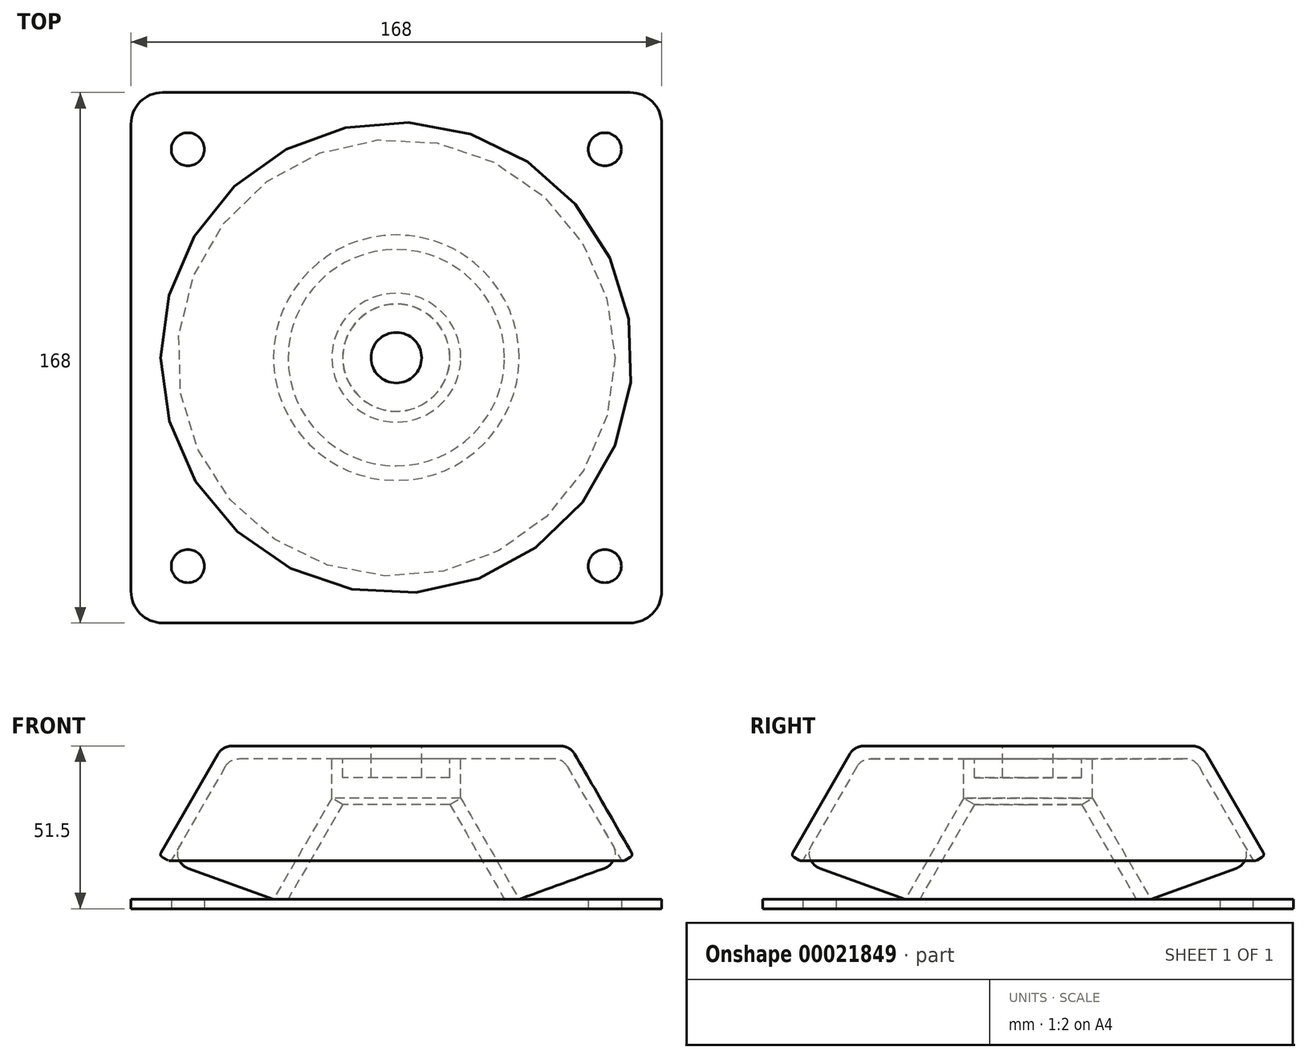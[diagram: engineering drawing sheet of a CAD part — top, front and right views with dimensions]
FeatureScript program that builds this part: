
annotation { "Feature Type Name" : "Feature", "Feature Type Description" : "" }
export const myFeature = defineFeature(function(context is Context, id is Id, definition is map)
    precondition{}
    {
        {
            var Q0;
            Q0=qCreatedBy(makeId("Top.planeOp"),FACE);
            var sketch = newSketch(context, id + "F0", { "sketchPlane" : qUnion([Q0])});
            skLineSegment(sketch, "E0.rect.bottom", {"start": v(-84, 84) * mm, "end": v(84, 84) * mm});
            skLineSegment(sketch, "E0.rect.top", {"start": v(-84, -84) * mm, "end": v(84, -84) * mm});
            skLineSegment(sketch, "E0.rect.left", {"start": v(-84, 84) * mm, "end": v(-84, -84) * mm});
            skLineSegment(sketch, "E0.rect.right", {"start": v(84, 84) * mm, "end": v(84, -84) * mm});
            skPoint(sketch, "E0.rect.middle", {"position": v(0, 0) * mm});
            skPoint(sketch, "E1", {"position": v(-66, 66) * mm});
            skPoint(sketch, "E2.MirrorP", {"position": v(66, 66) * mm});
            skPoint(sketch, "E3.MirrorP", {"position": v(-66, -66) * mm});
            skPoint(sketch, "E4.MirrorP", {"position": v(66, -66) * mm});
            skSolve(sketch);
        }
        {
            var Q0;
            Q0 = qSketchRegion(id + "F0", true);
            extrude(context, id + "F1", {"entities" : qUnion([Q0]), "depth" : 3 * mm});
        }
        {
            var Q0;
            Q0=sQuery(id+"F0.wireOp",VERTEX,"E1");
            var Q1;
            Q1=sQuery(id+"F0.wireOp",VERTEX,"E2.MirrorP");
            var Q2;
            Q2=sQuery(id+"F0.wireOp",VERTEX,"E4.MirrorP");
            var Q3;
            Q3=sQuery(id+"F0.wireOp",VERTEX,"E3.MirrorP");
            var Q4;
            Q4=makeQuery(id+"F1.opExtrude","SWEPT_BODY",BODY,{"disambiguationData":[OSD([sQuery(id+"F0.wireOp",EDGE,"E0.rect.bottom"),sQuery(id+"F0.wireOp",EDGE,"E0.rect.top"),sQuery(id+"F0.wireOp",EDGE,"E0.rect.left"),sQuery(id+"F0.wireOp",EDGE,"E0.rect.right")])]});
            hole(context, id + "F2", {"style" : HoleStyle.SIMPLE, "holeDiameter" : 10.5 * mm, "endStyle" : HoleEndStyle.THROUGH, "oppositeDirection" : true, "locations" : qUnion([Q0, Q1, Q2, Q3]), "scope" : qUnion([Q4])});
        }
        {
            var Q0;
            Q0=makeQuery(id+"F1.opExtrude","SWEPT_EDGE",EDGE,{"disambiguationData":[OSD([sQuery(id+"F0.wireOp",EDGE,"E0.rect.bottom"),sQuery(id+"F0.wireOp",EDGE,"E0.rect.left")])]});
            var Q1;
            Q1=makeQuery(id+"F1.opExtrude","SWEPT_EDGE",EDGE,{"disambiguationData":[OSD([sQuery(id+"F0.wireOp",EDGE,"E0.rect.top"),sQuery(id+"F0.wireOp",EDGE,"E0.rect.left")])]});
            var Q2;
            Q2=makeQuery(id+"F1.opExtrude","SWEPT_EDGE",EDGE,{"disambiguationData":[OSD([sQuery(id+"F0.wireOp",EDGE,"E0.rect.top"),sQuery(id+"F0.wireOp",EDGE,"E0.rect.right")])]});
            var Q3;
            Q3=makeQuery(id+"F1.opExtrude","SWEPT_EDGE",EDGE,{"disambiguationData":[OSD([sQuery(id+"F0.wireOp",EDGE,"E0.rect.bottom"),sQuery(id+"F0.wireOp",EDGE,"E0.rect.right")])]});
            fillet(context, id + "F3", {"entities" : qUnion([Q0, Q1, Q2, Q3]), "radius" : 10 * mm, "tangentPropagation" : true, "allowEdgeOverflow" : false});
        }
        {
            var Q0;
            Q0=qCreatedBy(makeId("Front.planeOp"),FACE);
            var sketch = newSketch(context, id + "F4", { "sketchPlane" : qUnion([Q0])});
            skLineSegment(sketch, "E5", {"start": v(-16.95, 33) * mm, "end": v(-36, 0) * mm});
            skLineSegment(sketch, "E6", {"start": v(-16.95, 33) * mm, "end": v(-20.41, 35) * mm});
            skLineSegment(sketch, "E7", {"start": v(-20.41, 35) * mm, "end": v(-38.89, 3) * mm});
            skLineSegment(sketch, "E8", {"start": v(-38.89, 3) * mm, "end": v(-36, 0) * mm});
            skLineSegment(sketch, "E9", {"start": v(0, 45.78) * mm, "end": v(0, -22.7) * mm, "construction": true});
            skSolve(sketch);
        }
        {
            var Q0;
            Q0=makeQuery(id+"F4.imprint","IMPRINT",FACE,{"disambiguationData":[TD([[makeQuery(id+"F4.imprint","IMPRINT",EDGE,{"derivedFrom":sQuery(id+"F4.wireOp",EDGE,"E5")}),-1.0]])]});
            var Q1;
            Q1=sQuery(id+"F4.wireOp",EDGE,"E9");
            revolve(context, id + "F5", {"operationType" : NewBodyOperationType.ADD, "entities" : qUnion([Q0]), "axis" : qUnion([Q1]), "revolveType" : RevolveType.FULL});
        }
        {
            var Q0;
            Q0=qCreatedBy(makeId("Front.planeOp"),FACE);
            var sketch = newSketch(context, id + "F6", { "sketchPlane" : qUnion([Q0])});
            skLineSegment(sketch, "E10", {"start": v(-75, 16.86) * mm, "end": v(-56.44, 49) * mm});
            skLineSegment(sketch, "E11", {"start": v(-17, 47.5) * mm, "end": v(-49.8, 47.5) * mm});
            skLineSegment(sketch, "E12", {"start": v(-54.13, 45) * mm, "end": v(-71.54, 14.86) * mm});
            skLineSegment(sketch, "E13", {"start": v(-71.54, 14.86) * mm, "end": v(-75, 16.86) * mm});
            skLineSegment(sketch, "E14", {"start": v(-52.11, 51.5) * mm, "end": v(-8, 51.5) * mm});
            skLineSegment(sketch, "E15", {"start": v(-8, 51.5) * mm, "end": v(-8, 41.5) * mm});
            skLineSegment(sketch, "E16", {"start": v(-8, 41.5) * mm, "end": v(-17, 41.5) * mm});
            skLineSegment(sketch, "E17", {"start": v(-17, 41.5) * mm, "end": v(-17, 47.5) * mm});
            skPoint(sketch, "E18.visualSharp", {"position": v(-52.7, 47.5) * mm});
            skArc(sketch, "E18.filletArc", {"start": v(-49.8, 47.5) * mm, "mid": v(-52.3, 46.83) * mm, "end": v(-54.13, 45) * mm});
            skPoint(sketch, "E19.visualSharp", {"position": v(-55, 51.5) * mm});
            skArc(sketch, "E19.filletArc", {"start": v(-52.11, 51.5) * mm, "mid": v(-54.61, 50.83) * mm, "end": v(-56.44, 49) * mm});
            skLineSegment(sketch, "E20", {"start": v(0, 51.56) * mm, "end": v(0, 20.22) * mm, "construction": true});
            skSolve(sketch);
        }
        {
            var Q0;
            Q0 = qSketchRegion(id + "F6", true);
            var Q1;
            Q1=sQuery(id+"F6.wireOp",EDGE,"E20");
            revolve(context, id + "F7", {"entities" : qUnion([Q0]), "axis" : qUnion([Q1]), "revolveType" : RevolveType.FULL});
        }
        {
            var Q0;
            Q0=qCreatedBy(makeId("Front.planeOp"),FACE);
            var sketch = newSketch(context, id + "F8", { "sketchPlane" : qUnion([Q0])});
            skLineSegment(sketch, "E21", {"start": v(-20.41, 35) * mm, "end": v(-20.41, 47.5) * mm});
            skLineSegment(sketch, "E22", {"start": v(-20.41, 47.5) * mm, "end": v(-49.8, 47.5) * mm});
            skLineSegment(sketch, "E23", {"start": v(-54.13, 45) * mm, "end": v(-71.54, 14.86) * mm});
            skLineSegment(sketch, "E24", {"start": v(-71.54, 14.86) * mm, "end": v(-38.89, 3) * mm});
            skLineSegment(sketch, "E25", {"start": v(-38.89, 3) * mm, "end": v(-20.41, 35) * mm});
            skPoint(sketch, "E26.visualSharp", {"position": v(-52.7, 47.5) * mm});
            skArc(sketch, "E26.filletArc", {"start": v(-49.8, 47.5) * mm, "mid": v(-52.3, 46.83) * mm, "end": v(-54.13, 45) * mm});
            skLineSegment(sketch, "E27", {"start": v(0, 45.12) * mm, "end": v(0, 9.23) * mm, "construction": true});
            skSolve(sketch);
        }
        {
            var Q0;
            Q0=makeQuery(id+"F8.imprint","IMPRINT",FACE,{"disambiguationData":[TD([[makeQuery(id+"F8.imprint","IMPRINT",EDGE,{"derivedFrom":sQuery(id+"F8.wireOp",EDGE,"E21")}),1.0]])]});
            var Q1;
            Q1=sQuery(id+"F8.wireOp",EDGE,"E27");
            revolve(context, id + "F9", {"entities" : qUnion([Q0]), "axis" : qUnion([Q1]), "revolveType" : RevolveType.FULL});
        }
        {
            var Q0;
            Q0=makeQuery(id+"F7.opRevolve","SWEPT_EDGE",EDGE,{"disambiguationData":[OSD([sQuery(id+"F6.wireOp",EDGE,"E10"),sQuery(id+"F6.wireOp",EDGE,"E13")])]});
            var Q1;
            Q1=makeQuery(id+"F7.opRevolve","SWEPT_EDGE",EDGE,{"disambiguationData":[OSD([sQuery(id+"F6.wireOp",EDGE,"E12"),sQuery(id+"F6.wireOp",EDGE,"E13")])]});
            fillet(context, id + "F10", {"entities" : qUnion([Q0, Q1]), "radius" : 1 * mm, "tangentPropagation" : true, "allowEdgeOverflow" : false});
        }
        {
            var Q0;
            Q0=makeQuery(id+"F9.opRevolve","SWEPT_EDGE",EDGE,{"disambiguationData":[OSD([sQuery(id+"F8.wireOp",EDGE,"E23"),sQuery(id+"F8.wireOp",EDGE,"E24")])]});
            fillet(context, id + "F11", {"entities" : qUnion([Q0]), "radius" : 5 * mm, "tangentPropagation" : true, "allowEdgeOverflow" : false});
        }
    });
